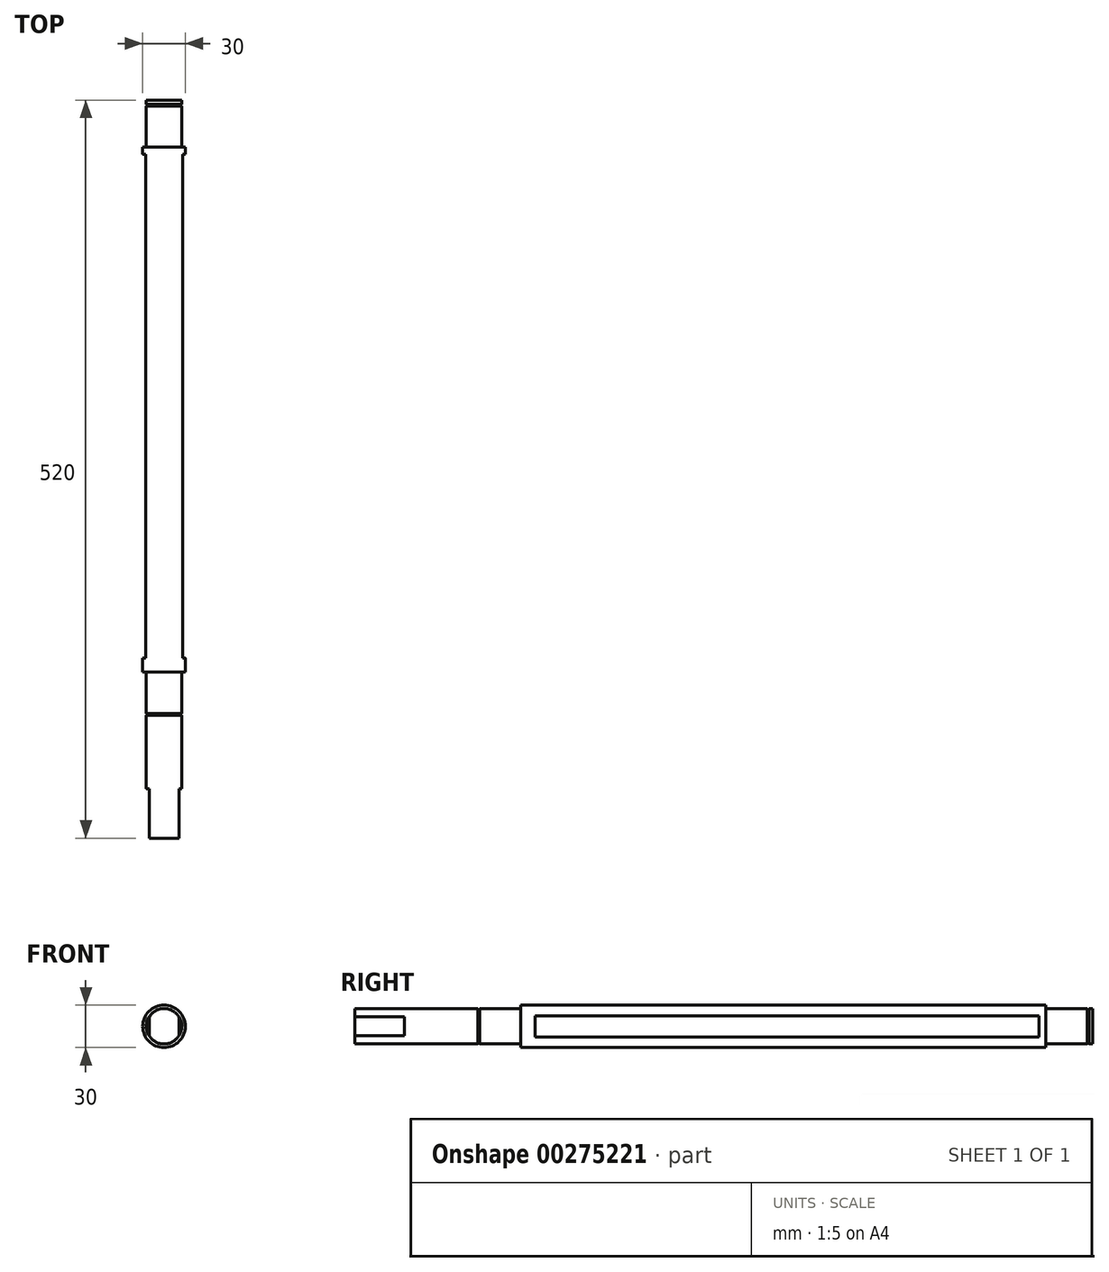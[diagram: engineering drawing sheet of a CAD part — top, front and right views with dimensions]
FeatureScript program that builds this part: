
annotation { "Feature Type Name" : "Feature", "Feature Type Description" : "" }
export const myFeature = defineFeature(function(context is Context, id is Id, definition is map)
    precondition{}
    {
        {
            var Q0;
            Q0=qCreatedBy(makeId("Right.planeOp"),FACE);
            var sketch = newSketch(context, id + "F0", { "sketchPlane" : qUnion([Q0])});
            skLineSegment(sketch, "E0.bottom", {"start": v(185, 15) * mm, "end": v(-185, 15) * mm});
            skLineSegment(sketch, "E0.top", {"start": v(185, -15) * mm, "end": v(-185, -15) * mm, "construction": true});
            skLineSegment(sketch, "E0.left", {"start": v(185, 15) * mm, "end": v(185, -15) * mm});
            skLineSegment(sketch, "E0.right", {"start": v(-185, 15) * mm, "end": v(-185, -15) * mm});
            skPoint(sketch, "E0.middle", {"position": v(0, 0) * mm});
            skLineSegment(sketch, "E1", {"start": v(185, -12.5) * mm, "end": v(214, -12.5) * mm, "construction": true});
            skLineSegment(sketch, "E2", {"start": v(218, -12.5) * mm, "end": v(218, 12.5) * mm});
            skLineSegment(sketch, "E3", {"start": v(218, 12.5) * mm, "end": v(215.3, 12.5) * mm});
            skLineSegment(sketch, "E4", {"start": v(214, 12.5) * mm, "end": v(214, 11.9) * mm});
            skLineSegment(sketch, "E5", {"start": v(214, 11.9) * mm, "end": v(215.3, 11.9) * mm});
            skLineSegment(sketch, "E6", {"start": v(215.3, 11.9) * mm, "end": v(215.3, 12.5) * mm});
            skLineSegment(sketch, "E7.trimOffspring", {"start": v(214, 12.5) * mm, "end": v(185, 12.5) * mm});
            skLineSegment(sketch, "E8.MirrorCS", {"start": v(214, -12.5) * mm, "end": v(214, -11.9) * mm, "construction": true});
            skLineSegment(sketch, "E9.MirrorCS", {"start": v(215.3, -11.9) * mm, "end": v(215.3, -12.5) * mm, "construction": true});
            skLineSegment(sketch, "E10.MirrorCS", {"start": v(214, -11.9) * mm, "end": v(215.3, -11.9) * mm, "construction": true});
            skLineSegment(sketch, "E11.trimOffspring", {"start": v(215.3, -12.5) * mm, "end": v(218, -12.5) * mm, "construction": true});
            skLineSegment(sketch, "E12", {"start": v(-185, 12.5) * mm, "end": v(-214, 12.5) * mm});
            skLineSegment(sketch, "E13", {"start": v(-302, 12.5) * mm, "end": v(-302, -12.5) * mm});
            skLineSegment(sketch, "E14", {"start": v(-302, -12.5) * mm, "end": v(-215.3, -12.5) * mm, "construction": true});
            skPoint(sketch, "E14.endSnap0", {"position": v(-185, 0) * mm});
            skLineSegment(sketch, "E15", {"start": v(-215.3, 12.5) * mm, "end": v(-215.3, 11.9) * mm});
            skLineSegment(sketch, "E16", {"start": v(-215.3, 11.9) * mm, "end": v(-214, 11.9) * mm});
            skLineSegment(sketch, "E17", {"start": v(-214, 11.9) * mm, "end": v(-214, 12.5) * mm});
            skLineSegment(sketch, "E18.MirrorCS", {"start": v(-215.3, -12.5) * mm, "end": v(-215.3, -11.9) * mm, "construction": true});
            skLineSegment(sketch, "E19.MirrorCS", {"start": v(-214, -11.9) * mm, "end": v(-214, -12.5) * mm, "construction": true});
            skLineSegment(sketch, "E20.MirrorCS", {"start": v(-215.3, -11.9) * mm, "end": v(-214, -11.9) * mm, "construction": true});
            skLineSegment(sketch, "E21.trimOffspring", {"start": v(-214, -12.5) * mm, "end": v(-185, -12.5) * mm, "construction": true});
            skLineSegment(sketch, "E22.trimOffspring", {"start": v(-215.3, 12.5) * mm, "end": v(-302, 12.5) * mm});
            skLineSegment(sketch, "E23", {"start": v(-308.18, 0) * mm, "end": v(246.34, 0) * mm});
            skSolve(sketch);
        }
        {
            var Q0;
            {var subQ6=sQuery(id+"F0.wireOp",EDGE,"E12");Q0=makeQuery(id+"F0.imprint","IMPRINT",FACE,{"disambiguationData":[TD([[makeQuery(id+"F0.imprint","IMPRINT",EDGE,{"derivedFrom":subQ6}),1.0]])]});}
            var Q1;
            {var subQ1=sQuery(id+"F0.wireOp",EDGE,"E0.bottom");Q1=makeQuery(id+"F0.imprint","IMPRINT",FACE,{"disambiguationData":[TD([[makeQuery(id+"F0.imprint","IMPRINT",EDGE,{"derivedFrom":subQ1}),1.0]])]});}
            var Q2;
            {var subQ0=sQuery(id+"F0.wireOp",EDGE,"E3");Q2=makeQuery(id+"F0.imprint","IMPRINT",FACE,{"disambiguationData":[TD([[makeQuery(id+"F0.imprint","IMPRINT",EDGE,{"derivedFrom":subQ0}),1.0]])]});}
            var Q3;
            Q3=sQuery(id+"F0.wireOp",EDGE,"E23");
            revolve(context, id + "F1", {"entities" : qUnion([Q0, Q1, Q2]), "axis" : qUnion([Q3]), "revolveType" : RevolveType.FULL});
        }
        {
            var Q0;
            Q0=makeQuery(id+"F1.opRevolve","SWEPT_FACE",FACE,{"disambiguationData":[OSD([sQuery(id+"F0.wireOp",EDGE,"E13")])]});
            var sketch = newSketch(context, id + "F2", { "sketchPlane" : qUnion([Q0])});
            skArc(sketch, "E24.0", {"start": v(-10.5, 6.78) * mm, "mid": v(-12.5, 0) * mm, "end": v(-10.5, -6.78) * mm});
            skLineSegment(sketch, "E25", {"start": v(10.5, 6.78) * mm, "end": v(10.5, -6.78) * mm});
            skArc(sketch, "E26.MirrorC", {"start": v(10.5, 6.78) * mm, "mid": v(12.5, 0) * mm, "end": v(10.5, -6.78) * mm});
            skLineSegment(sketch, "E27.MirrorCS", {"start": v(-10.5, 6.78) * mm, "end": v(-10.5, -6.78) * mm});
            skArc(sketch, "E28.trimOffspring", {"start": v(-10.5, -6.78) * mm, "mid": v(-12.5, 0) * mm, "end": v(-10.5, 6.78) * mm});
            skArc(sketch, "E29.trimOffspring", {"start": v(10.5, -6.78) * mm, "mid": v(12.5, 0) * mm, "end": v(10.5, 6.78) * mm});
            skSolve(sketch);
        }
        {
            var Q0;
            Q0=makeQuery(id+"F2.imprint","IMPRINT",FACE,{"disambiguationData":[TD([[makeQuery(id+"F2.imprint","IMPRINT",EDGE,{"derivedFrom":sQuery(id+"F2.wireOp",EDGE,"E27.MirrorCS")}),-1.0]])]});
            var Q1;
            Q1=makeQuery(id+"F2.imprint","IMPRINT",FACE,{"disambiguationData":[TD([[makeQuery(id+"F2.imprint","IMPRINT",EDGE,{"derivedFrom":sQuery(id+"F2.wireOp",EDGE,"E25")}),1.0]])]});
            extrude(context, id + "F3", {"entities" : qUnion([Q0, Q1]), "operationType" : NewBodyOperationType.REMOVE, "oppositeDirection" : true, "depth" : 35 * mm});
        }
        {
            var Q0;
            Q0=makeQuery(id+"F1.opRevolve","SWEPT_FACE",FACE,{"disambiguationData":[OSD([sQuery(id+"F0.wireOp",EDGE,"E0.left")])]});
            var sketch = newSketch(context, id + "F4", { "sketchPlane" : qUnion([Q0])});
            skArc(sketch, "E30.0", {"start": v(-13, 7.48) * mm, "mid": v(-15, 0) * mm, "end": v(-13, -7.48) * mm});
            skLineSegment(sketch, "E31", {"start": v(13, 7.48) * mm, "end": v(13, -7.48) * mm});
            skLineSegment(sketch, "E32.MirrorCS", {"start": v(-13, 7.48) * mm, "end": v(-13, -7.48) * mm});
            skArc(sketch, "E33.trimOffspring", {"start": v(13, -7.48) * mm, "mid": v(15, 0) * mm, "end": v(13, 7.48) * mm});
            skSolve(sketch);
        }
        {
            var Q0;
            Q0 = qSketchRegion(id + "F4", true);
            extrude(context, id + "F5", {"entities" : qUnion([Q0]), "operationType" : NewBodyOperationType.REMOVE, "oppositeDirection" : true, "depth" : 360 * mm, "hasSecondDirection" : true, "secondDirectionOppositeDirection" : true, "secondDirectionDepth" : 5 * mm});
        }
    });
